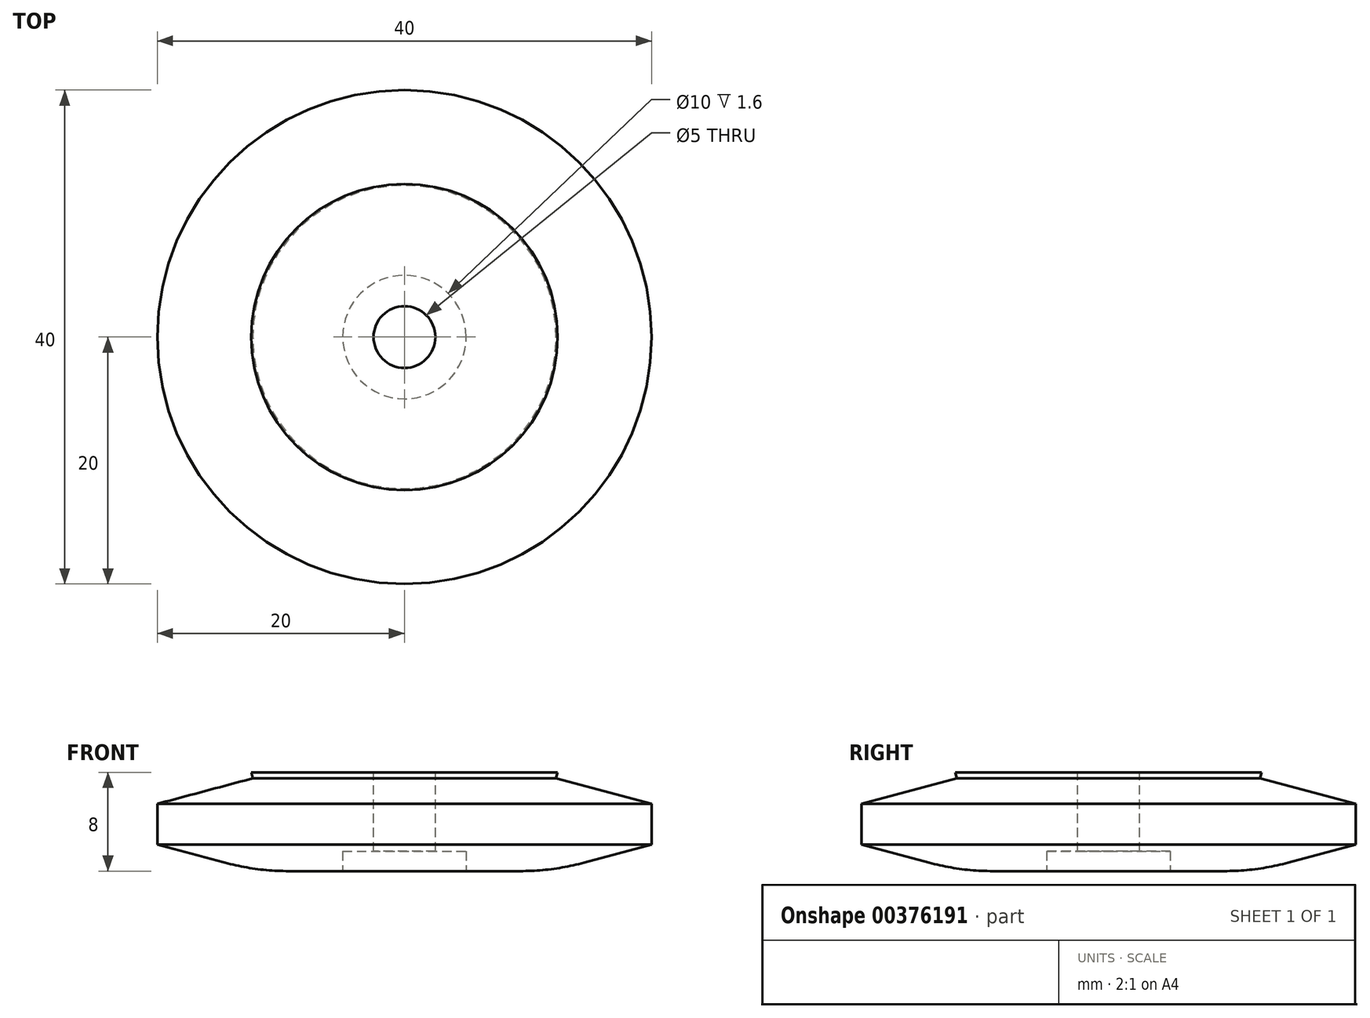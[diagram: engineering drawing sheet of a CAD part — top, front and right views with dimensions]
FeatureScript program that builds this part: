
annotation { "Feature Type Name" : "Feature", "Feature Type Description" : "" }
export const myFeature = defineFeature(function(context is Context, id is Id, definition is map)
    precondition{}
    {
        {
            var Q0;
            Q0=qCreatedBy(makeId("Front.planeOp"),FACE);
            var sketch = newSketch(context, id + "F0", { "sketchPlane" : qUnion([Q0])});
            skLineSegment(sketch, "E0", {"start": v(0, 0) * mm, "end": v(20, 0) * mm});
            skLineSegment(sketch, "E1", {"start": v(20, 0) * mm, "end": v(20, 5.45) * mm});
            skLineSegment(sketch, "E2", {"start": v(0, 0) * mm, "end": v(0, 8) * mm});
            skLineSegment(sketch, "E3", {"start": v(0, 8) * mm, "end": v(10.47, 8) * mm});
            skLineSegment(sketch, "E4", {"start": v(20, 5.45) * mm, "end": v(10.47, 8) * mm});
            skLineSegment(sketch, "E5", {"start": v(10.47, 8) * mm, "end": v(12.4, 8) * mm});
            skLineSegment(sketch, "E6", {"start": v(12.27, 7.52) * mm, "end": v(12.4, 8) * mm});
            skLineSegment(sketch, "E7", {"start": v(0, 0) * mm, "end": v(0, 1.6) * mm});
            skLineSegment(sketch, "E8", {"start": v(10, 1.6) * mm, "end": v(0, 1.6) * mm});
            skLineSegment(sketch, "E9", {"start": v(10, 1.6) * mm, "end": v(10, 0) * mm});
            skLineSegment(sketch, "E10", {"start": v(3, 8) * mm, "end": v(3, 0) * mm, "construction": true});
            skLineSegment(sketch, "E11", {"start": v(12, 0) * mm, "end": v(20, 2.14) * mm});
            skLineSegment(sketch, "E12", {"start": v(5, 1.6) * mm, "end": v(5, 0) * mm});
            skSolve(sketch);
        }
        {
            var Q0;
            {var subQ9=sQuery(id+"F0.wireOp",EDGE,"E9");Q0=makeQuery(id+"F0.imprint","IMPRINT",FACE,{"disambiguationData":[TD([[makeQuery(id+"F0.imprint","IMPRINT",EDGE,{"derivedFrom":subQ9}),1.0]])]});}
            var Q1;
            {var subQ0=sQuery(id+"F0.wireOp",EDGE,"E7");Q1=makeQuery(id+"F0.imprint","IMPRINT",FACE,{"disambiguationData":[TD([[makeQuery(id+"F0.imprint","IMPRINT",EDGE,{"derivedFrom":subQ0}),-1.0]])]});}
            var Q2;
            {var subQ0=sQuery(id+"F0.wireOp",EDGE,"E5");Q2=makeQuery(id+"F0.imprint","IMPRINT",FACE,{"disambiguationData":[TD([[makeQuery(id+"F0.imprint","IMPRINT",EDGE,{"derivedFrom":subQ0}),-1.0]])]});}
            var Q3;
            {var subQ0=sQuery(id+"F0.wireOp",EDGE,"E9");Q3=makeQuery(id+"F0.imprint","IMPRINT",FACE,{"disambiguationData":[TD([[makeQuery(id+"F0.imprint","IMPRINT",EDGE,{"derivedFrom":subQ0}),-1.0]])]});}
            var Q4;
            Q4=sQuery(id+"F0.wireOp",EDGE,"E2");
            revolve(context, id + "F1", {"entities" : qUnion([Q0, Q1, Q2, Q3]), "axis" : qUnion([Q4]), "revolveType" : RevolveType.FULL});
        }
        {
            var Q0;
            Q0=makeQuery(id+"F1.opRevolve","SWEPT_FACE",FACE,{"disambiguationData":[OSD([sQuery(id+"F0.wireOp",EDGE,"E3"),sQuery(id+"F0.wireOp",EDGE,"E5")])]});
            var sketch = newSketch(context, id + "F2", { "sketchPlane" : qUnion([Q0])});
            skPoint(sketch, "E13", {"position": v(0, 7) * mm});
            skPoint(sketch, "E14.MirrorP", {"position": v(0, -7) * mm});
            skPoint(sketch, "E15", {"position": v(-9, 0) * mm});
            skPoint(sketch, "E16.MirrorP", {"position": v(9, 0) * mm});
            skPoint(sketch, "E17", {"position": v(0, 0) * mm});
            skSolve(sketch);
        }
        {
            var Q0;
            Q0=sQuery(id+"F2.wireOp",VERTEX,"E17");
            var Q1;
            Q1=makeQuery(id+"F1.opRevolve","SWEPT_BODY",BODY,{"disambiguationData":[OSD([sQuery(id+"F0.wireOp",EDGE,"E0"),sQuery(id+"F0.wireOp",EDGE,"E1"),sQuery(id+"F0.wireOp",EDGE,"E2"),sQuery(id+"F0.wireOp",EDGE,"E3"),sQuery(id+"F0.wireOp",EDGE,"E4"),sQuery(id+"F0.wireOp",EDGE,"E5"),sQuery(id+"F0.wireOp",EDGE,"E6"),sQuery(id+"F0.wireOp",EDGE,"E8"),sQuery(id+"F0.wireOp",EDGE,"E9"),sQuery(id+"F0.wireOp",EDGE,"E11")])]});
            hole(context, id + "F3", {"style" : HoleStyle.SIMPLE, "endStyle" : HoleEndStyle.THROUGH, "standardTappedOrClearance" : lookupTablePath({ "standard" : "ISO", "engagement" : "75%", "pitch" : "1 mm", "size" : "M6", "type" : "Tapped" }), "standardBlindInLast" : lookupTablePath({ "standard" : "ISO", "engagement" : "75%", "pitch" : "1 mm", "size" : "M6", "type" : "Tapped" }), "holeDiameter" : 5 * mm, "showTappedDepth" : true, "isTappedThrough" : true, "tappedDepth" : 35 * mm, "tapClearance" : 3, "startFromSketch" : true, "locations" : qUnion([Q0]), "scope" : qUnion([Q1]), "majorDiameter" : 6 * mm});
        }
        {
            var Q0;
            Q0=makeQuery(id+"F1.opRevolve","SWEPT_EDGE",EDGE,{"disambiguationData":[OSD([sQuery(id+"F0.wireOp",EDGE,"E0"),sQuery(id+"F0.wireOp",EDGE,"E11")])]});
            fillet(context, id + "F4", {"entities" : qUnion([Q0]), "radius" : 20 * mm, "tangentPropagation" : true, "allowEdgeOverflow" : false});
        }
    });
